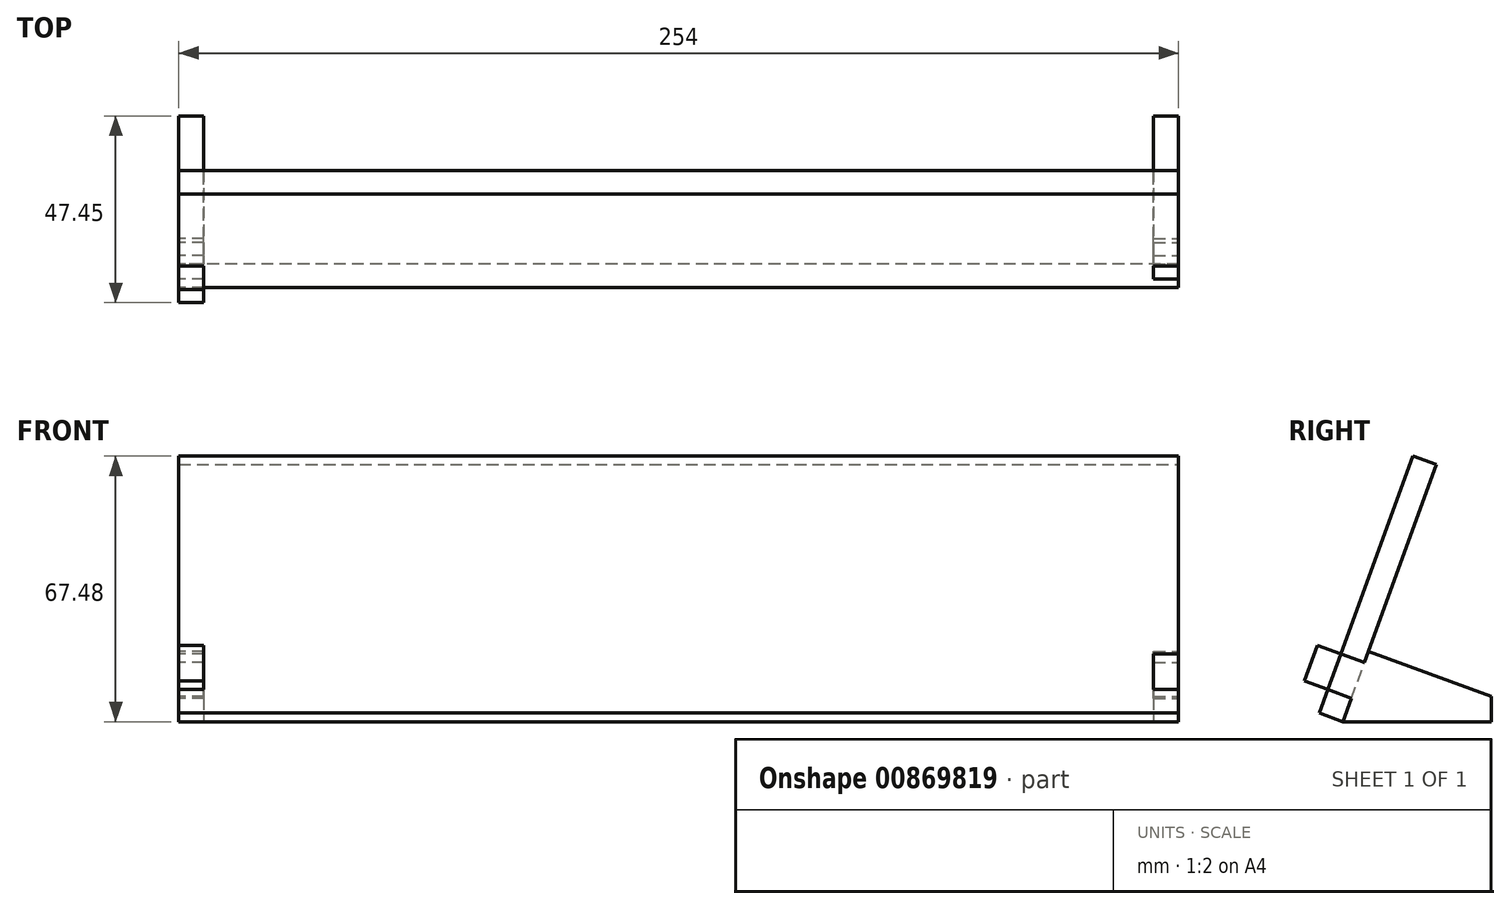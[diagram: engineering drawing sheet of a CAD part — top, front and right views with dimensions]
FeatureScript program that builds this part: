
annotation { "Feature Type Name" : "Feature", "Feature Type Description" : "" }
export const myFeature = defineFeature(function(context is Context, id is Id, definition is map)
    precondition{}
    {
        {
            var Q0;
            Q0=qCreatedBy(makeId("Top.planeOp"),FACE);
            var sketch = newSketch(context, id + "F0", { "sketchPlane" : qUnion([Q0])});
            skLineSegment(sketch, "E0.bottom", {"start": v(-127, 44.45) * mm, "end": v(-120.65, 44.45) * mm});
            skLineSegment(sketch, "E0.top", {"start": v(-127, 0) * mm, "end": v(-120.65, 0) * mm});
            skLineSegment(sketch, "E0.left", {"start": v(-127, 44.45) * mm, "end": v(-127, 0) * mm});
            skLineSegment(sketch, "E0.right", {"start": v(-120.65, 44.45) * mm, "end": v(-120.65, 0) * mm});
            skSolve(sketch);
        }
        {
            var Q0;
            Q0=makeQuery(id+"F0.imprint","IMPRINT",FACE,{"disambiguationData":[TD([[makeQuery(id+"F0.imprint","IMPRINT",EDGE,{"derivedFrom":sQuery(id+"F0.wireOp",EDGE,"E0.bottom")}),-1.0]])]});
            extrude(context, id + "F1", {"entities" : qUnion([Q0]), "depth" : 20 * mm, "offsetDistance" : 25 * mm});
        }
        {
            var Q0;
            Q0=makeQuery(id+"F1.opExtrude","SWEPT_FACE",FACE,{"disambiguationData":[OSD([sQuery(id+"F0.wireOp",EDGE,"E0.left")])]});
            var sketch = newSketch(context, id + "F2", { "sketchPlane" : qUnion([Q0])});
            skLineSegment(sketch, "E1", {"start": v(-7.28, 20) * mm, "end": v(-13.25, 17.83) * mm});
            skLineSegment(sketch, "E2", {"start": v(-13.25, 17.83) * mm, "end": v(-6.76, 0) * mm, "construction": true});
            skLineSegment(sketch, "E3", {"start": v(-0.8, 2.17) * mm, "end": v(-7.28, 20) * mm});
            skLineSegment(sketch, "E4", {"start": v(-13.25, 17.83) * mm, "end": v(-14.04, 20) * mm});
            skLineSegment(sketch, "E5", {"start": v(-14.04, 20) * mm, "end": v(0, 20) * mm});
            skLineSegment(sketch, "E6", {"start": v(0, 20) * mm, "end": v(0, 0) * mm});
            skLineSegment(sketch, "E7", {"start": v(-6.76, 0) * mm, "end": v(-0.8, 2.17) * mm});
            skLineSegment(sketch, "E8", {"start": v(-0.8, 2.17) * mm, "end": v(0, 0) * mm, "construction": true});
            skLineSegment(sketch, "E9", {"start": v(-6.76, 0) * mm, "end": v(0, 0) * mm});
            skLineSegment(sketch, "E10", {"start": v(-13.25, 17.83) * mm, "end": v(-44.45, 17.83) * mm});
            skLineSegment(sketch, "E11", {"start": v(-44.45, 17.83) * mm, "end": v(-44.45, 20) * mm});
            skLineSegment(sketch, "E12", {"start": v(-44.45, 20) * mm, "end": v(-14.04, 20) * mm});
            skLineSegment(sketch, "E13", {"start": v(-13.25, 17.83) * mm, "end": v(-44.45, 6.47) * mm});
            skLineSegment(sketch, "E14", {"start": v(-44.45, 6.47) * mm, "end": v(-44.45, 17.83) * mm});
            skLineSegment(sketch, "E15", {"start": v(-2.96, 8.14) * mm, "end": v(-8.93, 5.97) * mm});
            skLineSegment(sketch, "E16", {"start": v(-6.25, 17.18) * mm, "end": v(-12.22, 15) * mm});
            skLineSegment(sketch, "E17", {"start": v(-12.22, 15) * mm, "end": v(-13.25, 17.83) * mm});
            skLineSegment(sketch, "E18", {"start": v(-8.93, 5.97) * mm, "end": v(-6.76, 0) * mm});
            skSolve(sketch);
        }
        {
            var Q0;
            {var subQ0=sQuery(id+"F2.wireOp",EDGE,"E1");Q0=makeQuery(id+"F2.imprint","IMPRINT",FACE,{"disambiguationData":[TD([[makeQuery(id+"F2.imprint","IMPRINT",EDGE,{"derivedFrom":subQ0}),-1.0]])]});}
            var Q1;
            {var subQ0=sQuery(id+"F2.wireOp",EDGE,"E3");Q1=makeQuery(id+"F2.imprint","IMPRINT",FACE,{"disambiguationData":[TD([[makeQuery(id+"F2.imprint","IMPRINT",EDGE,{"derivedFrom":subQ0}),-1.0]])]});}
            var Q2;
            Q2=makeQuery(id+"F2.imprint","IMPRINT",FACE,{"disambiguationData":[TD([[makeQuery(id+"F2.imprint","IMPRINT",EDGE,{"derivedFrom":sQuery(id+"F2.wireOp",EDGE,"E4")}),1.0]])]});
            var Q3;
            Q3=makeQuery(id+"F2.imprint","IMPRINT",FACE,{"disambiguationData":[TD([[makeQuery(id+"F2.imprint","IMPRINT",EDGE,{"derivedFrom":sQuery(id+"F2.wireOp",EDGE,"E10")}),1.0]])]});
            var Q4;
            {var subQ0=sQuery(id+"F2.wireOp",EDGE,"E1");Q4=makeQuery(id+"F2.imprint","IMPRINT",FACE,{"disambiguationData":[TD([[makeQuery(id+"F2.imprint","IMPRINT",EDGE,{"derivedFrom":subQ0}),1.0]])]});}
            var Q5;
            {var subQ0=sQuery(id+"F2.wireOp",EDGE,"E7");Q5=makeQuery(id+"F2.imprint","IMPRINT",FACE,{"disambiguationData":[TD([[makeQuery(id+"F2.imprint","IMPRINT",EDGE,{"derivedFrom":subQ0}),1.0]])]});}
            var Q6;
            Q6=makeQuery(id+"F1.opExtrude","SWEPT_FACE",FACE,{"disambiguationData":[OSD([sQuery(id+"F0.wireOp",EDGE,"E0.right")])]});
            extrude(context, id + "F3", {"entities" : qUnion([Q0, Q1, Q2, Q3, Q4, Q5]), "operationType" : NewBodyOperationType.REMOVE, "endBound" : BoundingType.UP_TO_SURFACE, "oppositeDirection" : true, "depth" : 25 * mm, "endBoundEntityFace" : qUnion([Q6]), "offsetDistance" : 25 * mm});
        }
        {
            var Q0;
            Q0=makeQuery(id+"F1.opExtrude","SWEPT_BODY",BODY,{"disambiguationData":[OSD([sQuery(id+"F0.wireOp",EDGE,"E0.bottom"),sQuery(id+"F0.wireOp",EDGE,"E0.top"),sQuery(id+"F0.wireOp",EDGE,"E0.left"),sQuery(id+"F0.wireOp",EDGE,"E0.right")])]});
            var Q1;
            Q1=qCreatedBy(makeId("Right.planeOp"),FACE);
            mirror(context, id + "F4", {"entities" : qUnion([Q0]), "mirrorPlane" : qUnion([Q1])});
        }
        {
            var Q0;
            Q0=makeQuery(id+"F3.boolean.opBoolean","COPY",FACE,{"derivedFrom":makeQuery(id+"F3.opExtrude","SWEPT_FACE",FACE,{"disambiguationData":[OSD([sQuery(id+"F2.wireOp",EDGE,"E3")])]})});
            var sketch = newSketch(context, id + "F5", { "sketchPlane" : qUnion([Q0])});
            skLineSegment(sketch, "E19", {"start": v(120.65, 8.66) * mm, "end": v(120.65, 18.28) * mm});
            skLineSegment(sketch, "E20", {"start": v(-120.65, 8.66) * mm, "end": v(-120.65, 18.28) * mm});
            skLineSegment(sketch, "E21", {"start": v(-120.65, 18.28) * mm, "end": v(-127, 18.28) * mm});
            skLineSegment(sketch, "E22", {"start": v(-127, 18.28) * mm, "end": v(-127, 71.81) * mm});
            skLineSegment(sketch, "E23", {"start": v(-127, 71.81) * mm, "end": v(127, 71.81) * mm});
            skLineSegment(sketch, "E24", {"start": v(127, 71.81) * mm, "end": v(127, 18.28) * mm});
            skLineSegment(sketch, "E25", {"start": v(127, 18.28) * mm, "end": v(120.65, 18.28) * mm});
            skPoint(sketch, "E26.0", {"position": v(120.65, 18.28) * mm});
            skPoint(sketch, "E27.0", {"position": v(127, 18.28) * mm});
            skPoint(sketch, "E28.0", {"position": v(120.65, 8.66) * mm});
            skPoint(sketch, "E29.0", {"position": v(-127, 18.28) * mm});
            skPoint(sketch, "E30.0", {"position": v(-120.65, 2.31) * mm});
            skPoint(sketch, "E31.0", {"position": v(127, 21.28) * mm});
            skPoint(sketch, "E32.0", {"position": v(120.65, 2.31) * mm});
            skPoint(sketch, "E33.0", {"position": v(127, 2.31) * mm});
            skPoint(sketch, "E34.0", {"position": v(-127, 2.31) * mm});
            skLineSegment(sketch, "E35", {"start": v(-120.65, 8.66) * mm, "end": v(-127, 8.66) * mm});
            skLineSegment(sketch, "E36", {"start": v(-127, 8.66) * mm, "end": v(-127, 2.31) * mm});
            skLineSegment(sketch, "E37", {"start": v(127, 2.31) * mm, "end": v(-127, 2.31) * mm});
            skLineSegment(sketch, "E38", {"start": v(127, 2.31) * mm, "end": v(127, 8.66) * mm});
            skLineSegment(sketch, "E39", {"start": v(127, 8.66) * mm, "end": v(120.65, 8.66) * mm});
            skSolve(sketch);
        }
        {
            var Q0;
            Q0 = qSketchRegion(id + "F5", true);
            extrude(context, id + "F6", {"entities" : qUnion([Q0]), "oppositeDirection" : true, "depth" : 6.35 * mm, "offsetDistance" : 25 * mm});
        }
        {
            var Q0;
            Q0=makeQuery(id+"FRp4n8L0WyCwi7X_2.imprint","IMPRINT",FACE,{"disambiguationData":[TD([[makeQuery(id+"FRp4n8L0WyCwi7X_2.imprint","IMPRINT",EDGE,{"derivedFrom":sQuery(id+"FRp4n8L0WyCwi7X_2.wireOp",EDGE,"a1f58ee0-6030-4d5a-9bff-1619d3611d4d.0")}),-1.0]])]});
            var Q1;
            Q1=makeQuery(id+"F3.boolean.opBoolean","COPY",FACE,{"derivedFrom":makeQuery(id+"F3.opExtrude","SWEPT_FACE",FACE,{"disambiguationData":[OSD([sQuery(id+"F2.wireOp",EDGE,"E3")])]})});
            var Q2;
            Q2=makeQuery(id+"FRp4n8L0WyCwi7X_2.imprint","IMPRINT",FACE,{"disambiguationData":[TD([[makeQuery(id+"FRp4n8L0WyCwi7X_2.imprint","IMPRINT",EDGE,{"derivedFrom":sQuery(id+"FRp4n8L0WyCwi7X_2.wireOp",EDGE,"25d366cb-585b-4a4a-84e1-115fab61ac47.1")}),1.0]])]});
            extrude(context, id + "F7", {"entities" : qUnion([Q0, Q1, Q2]), "depth" : 6.35 * mm, "offsetDistance" : 25 * mm});
        }
    });
